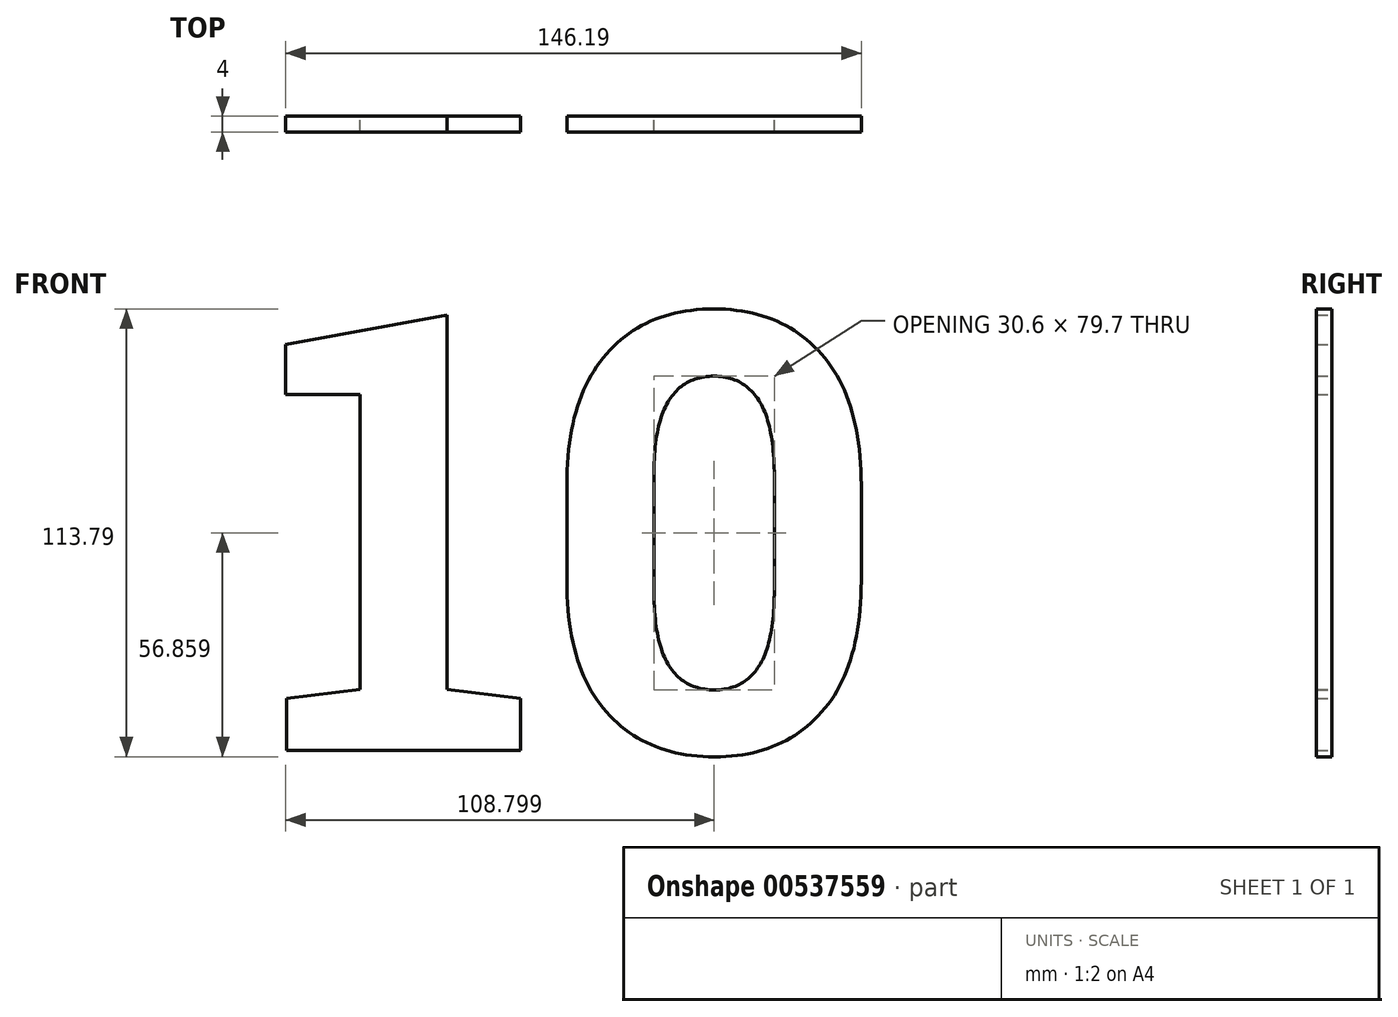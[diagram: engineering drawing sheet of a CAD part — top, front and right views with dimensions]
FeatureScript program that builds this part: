
annotation { "Feature Type Name" : "Feature", "Feature Type Description" : "" }
export const myFeature = defineFeature(function(context is Context, id is Id, definition is map)
    precondition{}
    {
        {
            var Q0;
            Q0=qCreatedBy(makeId("Front.planeOp"),FACE);
            var sketch = newSketch(context, id + "F0", { "sketchPlane" : qUnion([Q0])});
            skText(sketch, "E0", { "text": "10", "fontName": "RobotoSlab-Bold.ttf"});
            const initialGuessF0  = {"E0": [-0.07886, -0.0497, 1, 0, 0.112]};
            skSetInitialGuess(sketch, initialGuessF0);
            skSolve(sketch);
        }
        {
            var Q0;
            Q0 = qSketchRegion(id + "F0", true);
            extrude(context, id + "F1", {"entities" : qUnion([Q0]), "depth" : 4 * mm, "offsetDistance" : 25.4 * mm});
        }
    });
